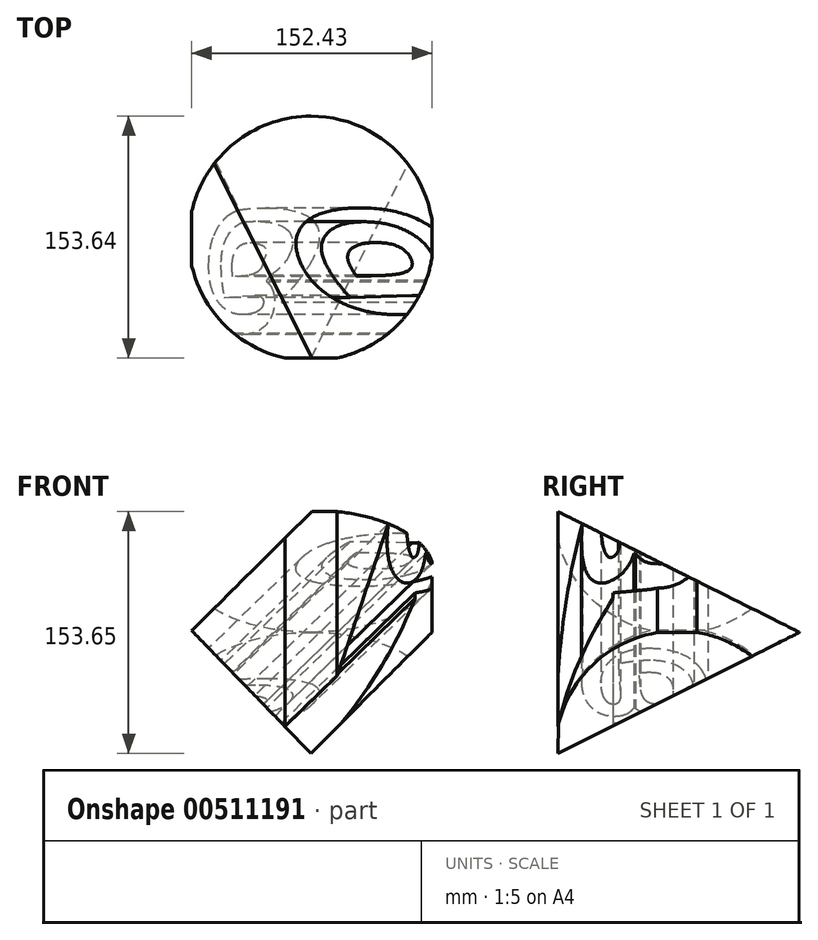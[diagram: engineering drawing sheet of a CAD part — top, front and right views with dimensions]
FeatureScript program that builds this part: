
annotation { "Feature Type Name" : "Feature", "Feature Type Description" : "" }
export const myFeature = defineFeature(function(context is Context, id is Id, definition is map)
    precondition{}
    {
        {
            var Q0;
            Q0=qCreatedBy(makeId("Front.planeOp"),FACE);
            var sketch = newSketch(context, id + "F0", { "sketchPlane" : qUnion([Q0])});
            skLineSegment(sketch, "E0.bottom", {"start": v(76.69, 76.75) * mm, "end": v(-75.74, 76.75) * mm});
            skLineSegment(sketch, "E0.top", {"start": v(76.69, -76.9) * mm, "end": v(-75.74, -76.9) * mm});
            skLineSegment(sketch, "E0.left", {"start": v(76.69, 76.75) * mm, "end": v(76.69, -76.9) * mm});
            skLineSegment(sketch, "E0.right", {"start": v(-75.74, 76.75) * mm, "end": v(-75.74, -76.9) * mm});
            skLineSegment(sketch, "E1.bottom", {"start": v(-75.74, 76.75) * mm, "end": v(76.69, 76.75) * mm});
            skLineSegment(sketch, "E1.top", {"start": v(-75.74, -76.9) * mm, "end": v(76.69, -76.9) * mm});
            skSolve(sketch);
        }
        {
            var Q0;
            Q0 = qSketchRegion(id + "F0", true);
            var Q1;
            Q1=sQuery(id+"F0.wireOp",EDGE,"E0.left");
            extrude(context, id + "F1", {"bodyType" : ToolBodyType.SURFACE, "surfaceEntities" : qUnion([Q0, Q1]), "depth" : 153.64 * mm});
        }
        {
            var Q0;
            Q0=makeQuery(id+"F1.opExtrude","CAP_FACE",FACE,{"disambiguationData":[OSD([sQuery(id+"F0.wireOp",EDGE,"E1.bottom"),sQuery(id+"F0.wireOp",EDGE,"E1.top"),sQuery(id+"F0.wireOp",EDGE,"E0.right"),sQuery(id+"F0.wireOp",EDGE,"E0.left")])],"isStart":false});
            var sketch = newSketch(context, id + "F2", { "sketchPlane" : qUnion([Q0])});
            skLineSegment(sketch, "E2", {"start": v(0.48, 76.75) * mm, "end": v(76.69, 0) * mm});
            skPoint(sketch, "E2.endSnap0", {"position": v(76.69, -0.08) * mm});
            skLineSegment(sketch, "E3", {"start": v(76.69, 0) * mm, "end": v(0.48, 76.75) * mm});
            skLineSegment(sketch, "E4", {"start": v(0.48, 76.75) * mm, "end": v(-75.74, 1.06) * mm});
            skPoint(sketch, "E4.endSnap0", {"position": v(-75.74, -0.08) * mm});
            skLineSegment(sketch, "E5", {"start": v(-75.74, 1.06) * mm, "end": v(0, -76.9) * mm});
            skPoint(sketch, "E5.endSnap0", {"position": v(0.48, -76.9) * mm});
            skLineSegment(sketch, "E6", {"start": v(0, -76.9) * mm, "end": v(76.69, -0.08) * mm});
            skSolve(sketch);
        }
        {
            var Q0;
            {var subQ0=sQuery(id+"F0.wireOp",EDGE,"E0.left");Q0=makeQuery(id+"F1.opExtrude","SWEPT_FACE",FACE,{"disambiguationData":[OSD([subQ0]),TDD([subQ0])]});}
            var sketch = newSketch(context, id + "F3", { "sketchPlane" : qUnion([Q0])});
            skLineSegment(sketch, "E7", {"start": v(153.64, 76.75) * mm, "end": v(153.64, -76.9) * mm});
            skLineSegment(sketch, "E8", {"start": v(153.64, -76.9) * mm, "end": v(0, 0) * mm});
            skLineSegment(sketch, "E9", {"start": v(0, 0) * mm, "end": v(153.64, 76.75) * mm});
            skSolve(sketch);
        }
        {
            var Q0;
            {var subQ0=sQuery(id+"F2.wireOp",EDGE,"E4");Q0=makeQuery(id+"F2.imprint","IMPRINT",FACE,{"disambiguationData":[TD([[makeQuery(id+"F2.imprint","IMPRINT",EDGE,{"derivedFrom":subQ0}),-1.0]])]});}
            var Q1;
            {var subQ0=sQuery(id+"F2.wireOp",EDGE,"E5");Q1=makeQuery(id+"F2.imprint","IMPRINT",FACE,{"disambiguationData":[TD([[makeQuery(id+"F2.imprint","IMPRINT",EDGE,{"derivedFrom":subQ0}),-1.0]])]});}
            var Q2;
            {var subQ0=sQuery(id+"F2.wireOp",EDGE,"E3");Q2=makeQuery(id+"F2.imprint","IMPRINT",FACE,{"disambiguationData":[TD([[makeQuery(id+"F2.imprint","IMPRINT",EDGE,{"derivedFrom":subQ0}),-1.0]])]});}
            var Q3;
            {var subQ0=sQuery(id+"F2.wireOp",EDGE,"E6");Q3=makeQuery(id+"F2.imprint","IMPRINT",FACE,{"disambiguationData":[TD([[makeQuery(id+"F2.imprint","IMPRINT",EDGE,{"derivedFrom":subQ0}),-1.0]])]});}
            extrude(context, id + "F4", {"entities" : qUnion([Q0, Q1, Q2, Q3]), "operationType" : NewBodyOperationType.REMOVE, "oppositeDirection" : true, "depth" : 154.4 * mm, "offsetDistance" : 25.4 * mm});
        }
        {
            var Q0;
            {var subQ0=sQuery(id+"F3.wireOp",EDGE,"E9");Q0=makeQuery(id+"F3.imprint","IMPRINT",FACE,{"disambiguationData":[TD([[makeQuery(id+"F3.imprint","IMPRINT",EDGE,{"derivedFrom":subQ0}),1.0]])]});}
            var Q1;
            {var subQ0=sQuery(id+"F3.wireOp",EDGE,"E8");Q1=makeQuery(id+"F3.imprint","IMPRINT",FACE,{"disambiguationData":[TD([[makeQuery(id+"F3.imprint","IMPRINT",EDGE,{"derivedFrom":subQ0}),1.0]])]});}
            extrude(context, id + "F5", {"entities" : qUnion([Q0, Q1]), "operationType" : NewBodyOperationType.REMOVE, "depth" : 154.4 * mm, "offsetDistance" : 25.4 * mm});
        }
        {
            var Q0;
            Q0=makeQuery(id+"F1.opExtrude","SWEPT_BODY",BODY,{"disambiguationData":[OSD([sQuery(id+"F0.wireOp",EDGE,"E0.left")])]});
            deleteBodies(context, id + "F6", {"entities" : qUnion([Q0])});
        }
        {
            var Q0;
            Q0=qCreatedBy(makeId("Top.planeOp"),FACE);
            var sketch = newSketch(context, id + "F7", { "sketchPlane" : qUnion([Q0])});
            skCircle(sketch, "E10", {"center": v(0, -77.71) * mm, "radius": 77.71 * mm});
            skSolve(sketch);
        }
        {
            var Q0;
            Q0=makeQuery(id+"F7.imprint","IMPRINT",FACE,{"disambiguationData":[TD([[makeQuery(id+"F7.imprint","IMPRINT",EDGE,{"derivedFrom":sQuery(id+"F7.wireOp",EDGE,"E10")}),1.0]])]});
            var sketch = newSketch(context, id + "F8", { "sketchPlane" : qUnion([Q0])});
            skLineSegment(sketch, "E11.bottom", {"start": v(-108.51, -192.44) * mm, "end": v(108.51, -192.44) * mm});
            skLineSegment(sketch, "E11.top", {"start": v(-108.51, 41.42) * mm, "end": v(108.51, 41.42) * mm});
            skLineSegment(sketch, "E11.left", {"start": v(-108.51, -192.44) * mm, "end": v(-108.51, 41.42) * mm});
            skLineSegment(sketch, "E11.right", {"start": v(108.51, -192.44) * mm, "end": v(108.51, 41.42) * mm});
            skPoint(sketch, "E11.middle", {"position": v(0, -75.51) * mm});
            skSolve(sketch);
        }
        {
            var Q0;
            Q0=makeQuery(id+"F8.imprint","IMPRINT",FACE,{"disambiguationData":[TD([[makeQuery(id+"F8.imprint","IMPRINT",EDGE,{"derivedFrom":sQuery(id+"F8.wireOp",EDGE,"E11.bottom")}),1.0]])]});
            extrude(context, id + "F9", {"entities" : qUnion([Q0]), "operationType" : NewBodyOperationType.REMOVE, "oppositeDirection" : true, "depth" : 101.6 * mm, "offsetDistance" : 25.4 * mm, "hasSecondDirection" : true, "secondDirectionOppositeDirection" : false, "secondDirectionDepth" : 101.6 * mm});
        }
        {
            var Q0;
            Q0=makeQuery(id+"F4.boolean.opBoolean","COPY",FACE,{"derivedFrom":makeQuery(id+"F4.opExtrude","SWEPT_FACE",FACE,{"disambiguationData":[OSD([sQuery(id+"F2.wireOp",EDGE,"E5")])]})});
            var sketch = newSketch(context, id + "F10", { "sketchPlane" : qUnion([Q0])});
            skText(sketch, "E12", { "text": "@", "fontName": "OpenSans-Bold.ttf"});
            const initialGuessF10  = {"E12": [0.03985, -0.03544, 1, 0, 0.0839]};
            skSetInitialGuess(sketch, initialGuessF10);
            skSolve(sketch);
        }
        {
            var Q0;
            {var subQ0=sQuery(id+"F10.wireOp",EDGE,"E12.sketch_text.stroke-39");Q0=makeQuery(id+"F10.imprint","IMPRINT",FACE,{"disambiguationData":[TD([[makeQuery(id+"F10.imprint","IMPRINT",EDGE,{"derivedFrom":subQ0}),1.0]])]});}
            var Q1;
            {var subQ0=sQuery(id+"F10.wireOp",EDGE,"E12.sketch_text.stroke-38");var subQ1=sQuery(id+"F10.wireOp",EDGE,"E12.sketch_text.stroke-37");var subQ2=makeQuery(id+"F10.imprint","INTERSECT",VERTEX,{"derivedFrom":[subQ1,subQ0]});Q1=makeQuery(id+"F10.imprint","IMPRINT",FACE,{"disambiguationData":[TD([[makeQuery(id+"F10.imprint","IMPRINT",EDGE,{"disambiguationData":[TD([[subQ2,1.0]])],"derivedFrom":subQ1}),1.0]])]});}
            var Q2;
            {var subQ7=sQuery(id+"F10.wireOp",EDGE,"E12.sketch_text.stroke-7");Q2=makeQuery(id+"F10.imprint","IMPRINT",FACE,{"disambiguationData":[TD([[makeQuery(id+"F10.imprint","IMPRINT",EDGE,{"derivedFrom":subQ7}),1.0]])]});}
            var Q3;
            {var subQ5=sQuery(id+"F10.wireOp",EDGE,"E12.sketch_text.stroke-10");Q3=makeQuery(id+"F10.imprint","IMPRINT",FACE,{"disambiguationData":[TD([[makeQuery(id+"F10.imprint","IMPRINT",EDGE,{"derivedFrom":subQ5}),1.0]])]});}
            var Q4;
            {var subQ13=sQuery(id+"F10.wireOp",EDGE,"E12.sketch_text.stroke-0");Q4=makeQuery(id+"F10.imprint","IMPRINT",FACE,{"disambiguationData":[TD([[makeQuery(id+"F10.imprint","IMPRINT",EDGE,{"derivedFrom":subQ13}),1.0]])]});}
            extrude(context, id + "F11", {"entities" : qUnion([Q0, Q1, Q2, Q3, Q4]), "operationType" : NewBodyOperationType.REMOVE, "oppositeDirection" : true, "depth" : 177.8 * mm, "offsetDistance" : 25.4 * mm});
        }
    });
